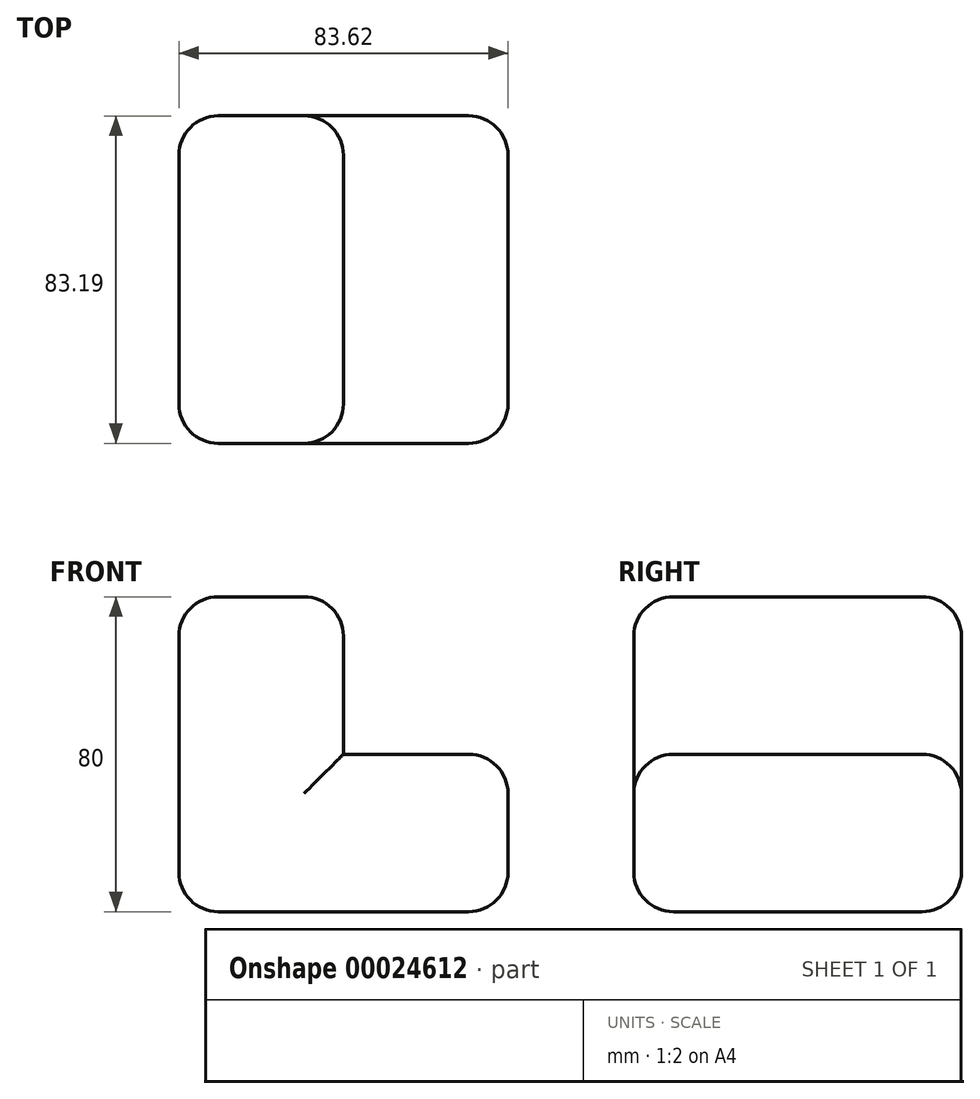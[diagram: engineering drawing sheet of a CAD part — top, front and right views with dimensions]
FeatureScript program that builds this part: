
annotation { "Feature Type Name" : "Feature", "Feature Type Description" : "" }
export const myFeature = defineFeature(function(context is Context, id is Id, definition is map)
    precondition{}
    {
        {
            var Q0;
            Q0=qCreatedBy(makeId("Top.planeOp"),FACE);
            var sketch = newSketch(context, id + "F0", { "sketchPlane" : qUnion([Q0])});
            skLineSegment(sketch, "E0.bottom", {"start": v(-59.13, -45.93) * mm, "end": v(24.5, -45.93) * mm});
            skLineSegment(sketch, "E0.top", {"start": v(-59.13, 37.26) * mm, "end": v(24.5, 37.26) * mm});
            skLineSegment(sketch, "E0.left", {"start": v(-59.13, -45.93) * mm, "end": v(-59.13, 37.26) * mm});
            skLineSegment(sketch, "E0.right", {"start": v(24.5, -45.93) * mm, "end": v(24.5, 37.26) * mm});
            skSolve(sketch);
        }
        {
            var Q0;
            Q0=makeQuery(id+"F0.imprint","IMPRINT",FACE,{"disambiguationData":[TD([[makeQuery(id+"F0.imprint","IMPRINT",EDGE,{"derivedFrom":sQuery(id+"F0.wireOp",EDGE,"E0.bottom")}),1.0]])]});
            extrude(context, id + "F1", {"entities" : qUnion([Q0]), "depth" : 40 * mm});
        }
        {
            var Q0;
            Q0=makeQuery(id+"F1.opExtrude","CAP_FACE",FACE,{"disambiguationData":[OSD([sQuery(id+"F0.wireOp",EDGE,"E0.bottom"),sQuery(id+"F0.wireOp",EDGE,"E0.top"),sQuery(id+"F0.wireOp",EDGE,"E0.left"),sQuery(id+"F0.wireOp",EDGE,"E0.right")])],"isStart":false});
            var sketch = newSketch(context, id + "F2", { "sketchPlane" : qUnion([Q0])});
            skLineSegment(sketch, "E1", {"start": v(-17.32, 37.26) * mm, "end": v(-17.32, -45.93) * mm});
            skSolve(sketch);
        }
        {
            var Q0;
            {var subQ1=sQuery(id+"F2.wireOp",EDGE,"E1");Q0=makeQuery(id+"F2.imprint","IMPRINT",FACE,{"disambiguationData":[TD([[makeQuery(id+"F2.imprint","IMPRINT",EDGE,{"derivedFrom":subQ1}),-1.0]])]});}
            extrude(context, id + "F3", {"entities" : qUnion([Q0]), "operationType" : NewBodyOperationType.ADD, "depth" : 40 * mm});
        }
        {
            var Q0;
            Q0=makeQuery(id+"F3.opExtrude","CAP_FACE",FACE,{"disambiguationData":[OSD([sQuery(id+"F0.wireOp",EDGE,"E0.bottom"),sQuery(id+"F0.wireOp",EDGE,"E0.top"),sQuery(id+"F0.wireOp",EDGE,"E0.left"),sQuery(id+"F2.wireOp",EDGE,"E1")])],"isStart":false});
            var Q1;
            Q1=makeQuery(id+"F3.opExtrude","SWEPT_EDGE",EDGE,{"disambiguationData":[OSD([sQuery(id+"F0.wireOp",EDGE,"E0.bottom"),sQuery(id+"F2.wireOp",EDGE,"E1")])]});
            var Q2;
            Q2=makeQuery(id+"F3.opExtrude","SWEPT_EDGE",EDGE,{"disambiguationData":[OSD([sQuery(id+"F0.wireOp",EDGE,"E0.top"),sQuery(id+"F2.wireOp",EDGE,"E1")])]});
            var Q3;
            Q3=makeQuery(id+"F1.opExtrude","CAP_EDGE",EDGE,{"disambiguationData":[OSD([sQuery(id+"F0.wireOp",EDGE,"E0.bottom")])],"isStart":false});
            var Q4;
            Q4=makeQuery(id+"F1.opExtrude","SWEPT_FACE",FACE,{"disambiguationData":[OSD([sQuery(id+"F0.wireOp",EDGE,"E0.right")])]});
            var Q5;
            Q5=makeQuery(id+"F1.opExtrude","CAP_EDGE",EDGE,{"disambiguationData":[OSD([sQuery(id+"F0.wireOp",EDGE,"E0.bottom")])],"isStart":true});
            var Q6;
            {var subQ0=sQuery(id+"F0.wireOp",EDGE,"E0.bottom");var subQ1=sQuery(id+"F0.wireOp",EDGE,"E0.left");Q6=makeQuery(id+"F3.boolean.opBoolean","MERGE",EDGE,{"derivedFrom":[makeQuery(id+"F1.opExtrude","SWEPT_EDGE",EDGE,{"disambiguationData":[OSD([subQ0,subQ1])]}),makeQuery(id+"F3.opExtrude","SWEPT_EDGE",EDGE,{"disambiguationData":[OSD([subQ0,subQ1])]})]});}
            var Q7;
            Q7=makeQuery(id+"F1.opExtrude","CAP_EDGE",EDGE,{"disambiguationData":[OSD([sQuery(id+"F0.wireOp",EDGE,"E0.top")])],"isStart":false});
            var Q8;
            Q8=makeQuery(id+"F1.opExtrude","CAP_EDGE",EDGE,{"disambiguationData":[OSD([sQuery(id+"F0.wireOp",EDGE,"E0.top")])],"isStart":true});
            var Q9;
            {var subQ0=sQuery(id+"F0.wireOp",EDGE,"E0.top");var subQ1=sQuery(id+"F0.wireOp",EDGE,"E0.left");Q9=makeQuery(id+"F3.boolean.opBoolean","MERGE",EDGE,{"derivedFrom":[makeQuery(id+"F1.opExtrude","SWEPT_EDGE",EDGE,{"disambiguationData":[OSD([subQ0,subQ1])]}),makeQuery(id+"F3.opExtrude","SWEPT_EDGE",EDGE,{"disambiguationData":[OSD([subQ0,subQ1])]})]});}
            var Q10;
            Q10=makeQuery(id+"F1.opExtrude","CAP_EDGE",EDGE,{"disambiguationData":[OSD([sQuery(id+"F0.wireOp",EDGE,"E0.left")])],"isStart":true});
            fillet(context, id + "F4", {"entities" : qUnion([Q0, Q1, Q2, Q3, Q4, Q5, Q6, Q7, Q8, Q9, Q10]), "radius" : 10 * mm, "tangentPropagation" : true, "allowEdgeOverflow" : false});
        }
    });
